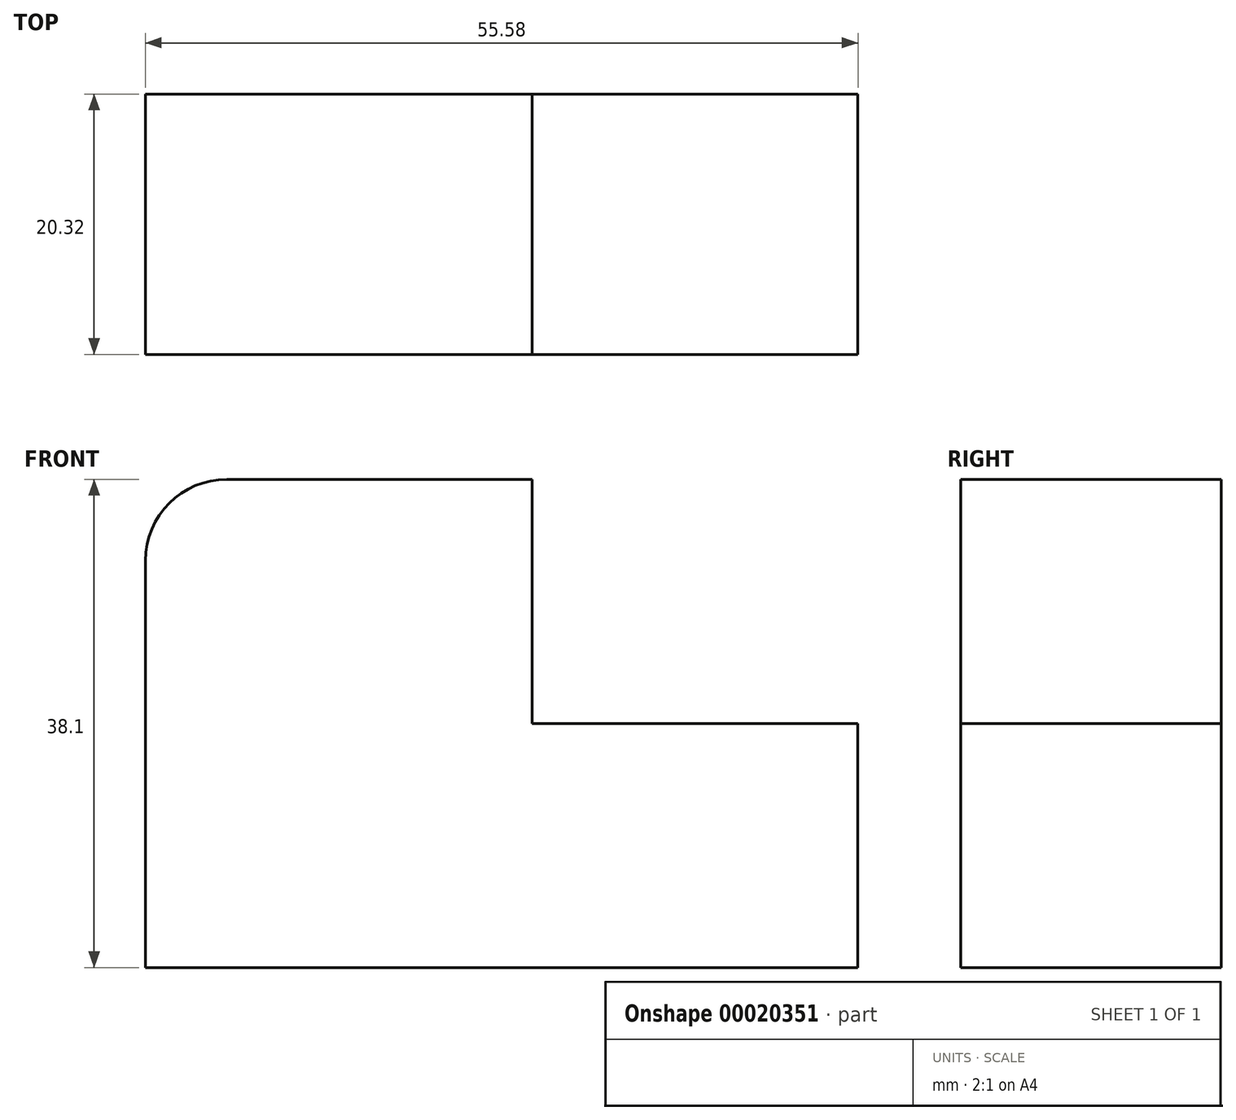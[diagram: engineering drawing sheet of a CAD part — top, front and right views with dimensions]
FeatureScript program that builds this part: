
annotation { "Feature Type Name" : "Feature", "Feature Type Description" : "" }
export const myFeature = defineFeature(function(context is Context, id is Id, definition is map)
    precondition{}
    {
        {
            var Q0;
            Q0=qCreatedBy(makeId("Front.planeOp"),FACE);
            var sketch = newSketch(context, id + "F0", { "sketchPlane" : qUnion([Q0])});
            skLineSegment(sketch, "E0.rect.bottom", {"start": v(-21.44, 19.05) * mm, "end": v(2.39, 19.05) * mm});
            skLineSegment(sketch, "E0.rect.top", {"start": v(-27.79, -19.05) * mm, "end": v(27.79, -19.05) * mm});
            skLineSegment(sketch, "E0.rect.left", {"start": v(-27.79, 12.7) * mm, "end": v(-27.79, -19.05) * mm});
            skLineSegment(sketch, "E0.rect.right", {"start": v(27.79, 0) * mm, "end": v(27.79, -19.05) * mm});
            skPoint(sketch, "E0.rect.middle", {"position": v(0, 0) * mm});
            skLineSegment(sketch, "E1.top", {"start": v(27.79, 0) * mm, "end": v(2.39, 0) * mm});
            skLineSegment(sketch, "E1.right", {"start": v(2.39, 19.05) * mm, "end": v(2.39, 0) * mm});
            skPoint(sketch, "E2.visualSharp", {"position": v(-27.79, 19.05) * mm});
            skArc(sketch, "E2.filletArc", {"start": v(-21.44, 19.05) * mm, "mid": v(-25.93, 17.2) * mm, "end": v(-27.79, 12.7) * mm});
            skSolve(sketch);
        }
        {
            var Q0;
            Q0=makeQuery(id+"F0.imprint","IMPRINT",FACE,{"disambiguationData":[TD([[makeQuery(id+"F0.imprint","IMPRINT",EDGE,{"derivedFrom":sQuery(id+"F0.wireOp",EDGE,"E0.rect.bottom")}),-1.0]])]});
            extrude(context, id + "F1", {"entities" : qUnion([Q0]), "depth" : 20.32 * mm});
        }
    });
